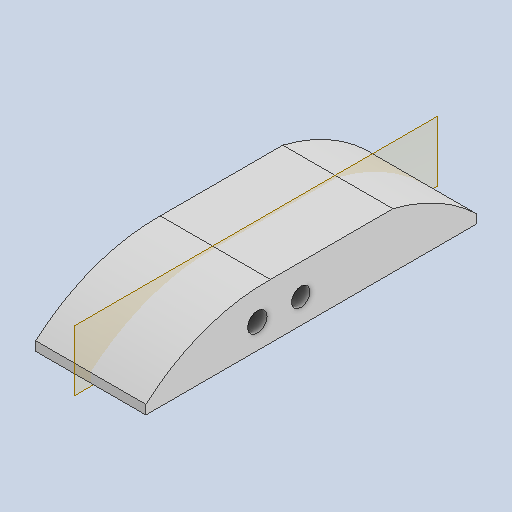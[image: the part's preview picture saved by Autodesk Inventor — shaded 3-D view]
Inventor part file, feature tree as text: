
AUTODESK INVENTOR PART (.ipt)
format: ipt  version: 2025 (Build 290162000, 162)  size: 139,776 bytes
history: native  units: in
note: dims shown in document units (in); Inventor stores cm internally (conversion verified against a paired STEP export)
features: sketch x5, extrude x4, other x2, plane x1, reference x1
ambient origin geometry x8: Origin, YZ Plane, XZ Plane, XY Plane, X Axis, Y Axis, Z Axis, Center Point
bodies: Solid1 (feature_tree)
feature tree (13):
  extrude  "Extrusion1"  Depth=3.0in
  extrude  "Extrusion2"  Depth=0.5in
  plane  "Work Plane1"
  extrude  "Extrusion4"  Depth=0.5in
  extrude  "Extrusion5"  Depth=3.0in
  sketch  "Sketch1"  dims[d0=13.0in d1=3.0in]
  sketch  "Sketch3"  dims[d5=3.0in d6=0.5in]
  sketch  "Sketch Rectangular Pattern1"  dims[d2=2.0in d3=0.5in]
  sketch  "Sketch5"  dims[d9=6.0in d10=3.0in]
  reference  "Reference1"
  sketch  "Sketch6"  dims[d11=6.0in d12=6.0in d13=0.0in d14=0.236in d15=0.25in d16=3.0in d17=0.7874in d19=5.5in d20=1.1811in d22=6.0in d25=0.5in d26=0.0in d37=10.0in d38=10.0in d39=0.0in d40=0.0in d41=1.0in d42=0.0in d43=0.0in]
  other  "UAV_Assembly.iam"
  other  "MiddleWingL_MIR:1"
